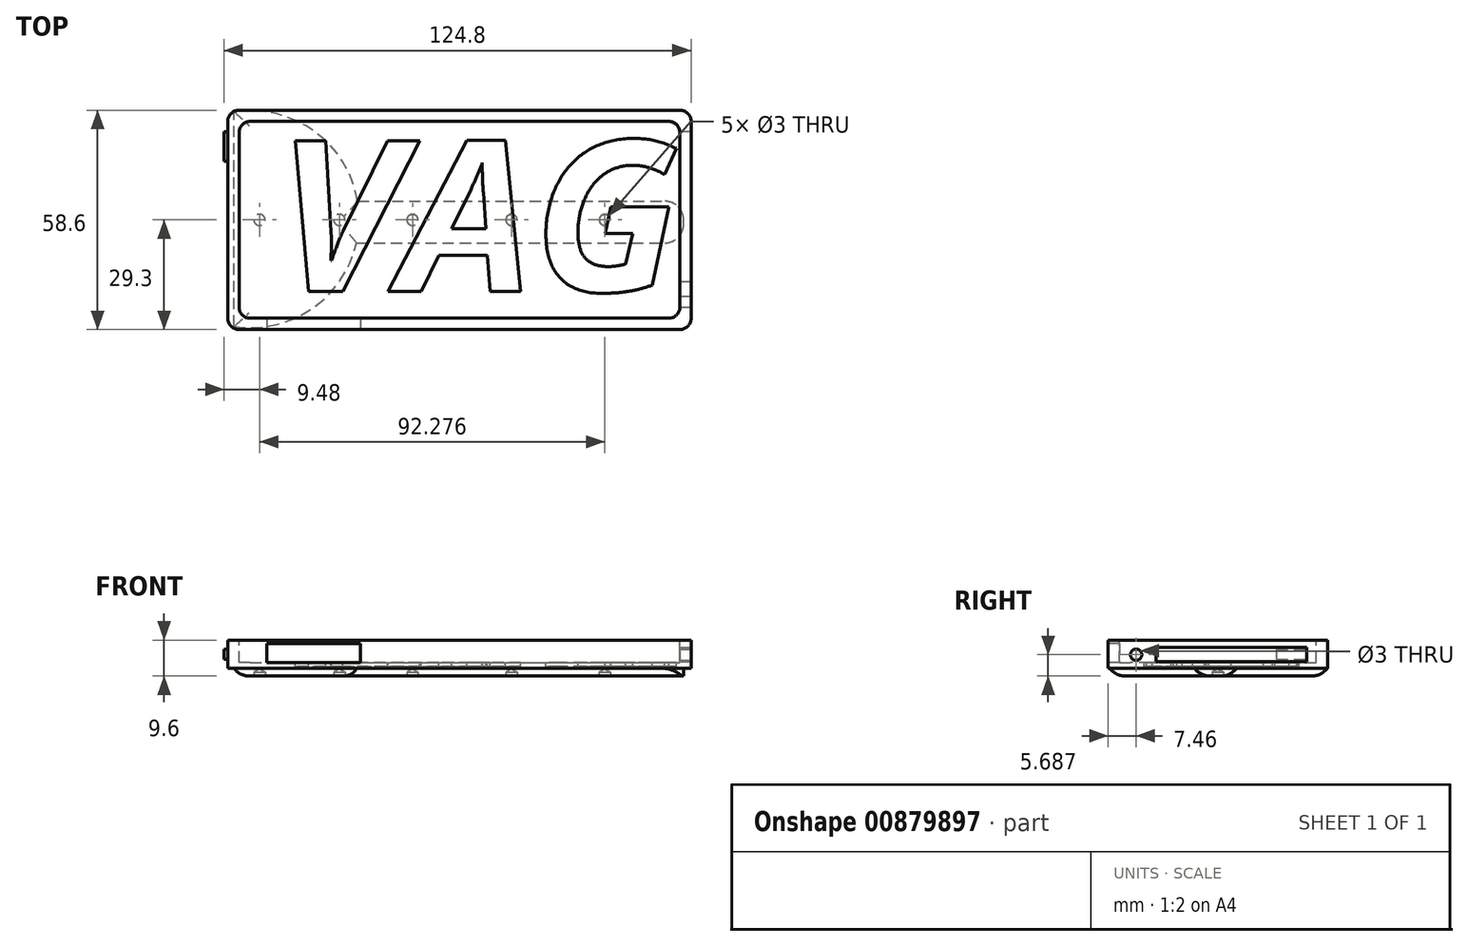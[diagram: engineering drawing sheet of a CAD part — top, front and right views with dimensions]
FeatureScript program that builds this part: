
annotation { "Feature Type Name" : "Feature", "Feature Type Description" : "" }
export const myFeature = defineFeature(function(context is Context, id is Id, definition is map)
    precondition{}
    {
        {
            var Q0;
            Q0=qCreatedBy(makeId("Top.planeOp"),FACE);
            var sketch = newSketch(context, id + "F0", { "sketchPlane" : qUnion([Q0])});
            skLineSegment(sketch, "E0.bottom", {"start": v(-118.8, 29.3) * mm, "end": v(-1, 29.3) * mm});
            skLineSegment(sketch, "E0.top", {"start": v(-118.8, -29.3) * mm, "end": v(-1, -29.3) * mm});
            skLineSegment(sketch, "E0.left", {"start": v(-121.8, 26.3) * mm, "end": v(-121.8, -26.3) * mm});
            skLineSegment(sketch, "E0.right", {"start": v(2, 26.3) * mm, "end": v(2, -26.3) * mm});
            skPoint(sketch, "E1.visualSharp", {"position": v(-121.8, 29.3) * mm});
            skArc(sketch, "E1.filletArc", {"start": v(-118.8, 29.3) * mm, "mid": v(-120.92, 28.42) * mm, "end": v(-121.8, 26.3) * mm});
            skPoint(sketch, "E2.visualSharp", {"position": v(2, 29.3) * mm});
            skArc(sketch, "E2.filletArc", {"start": v(2, 26.3) * mm, "mid": v(1.12, 28.42) * mm, "end": v(-1, 29.3) * mm});
            skPoint(sketch, "E3.visualSharp", {"position": v(2, -29.3) * mm});
            skArc(sketch, "E3.filletArc", {"start": v(-1, -29.3) * mm, "mid": v(1.12, -28.42) * mm, "end": v(2, -26.3) * mm});
            skPoint(sketch, "E4.visualSharp", {"position": v(-121.8, -29.3) * mm});
            skArc(sketch, "E4.filletArc", {"start": v(-121.8, -26.3) * mm, "mid": v(-120.92, -28.42) * mm, "end": v(-118.8, -29.3) * mm});
            skSolve(sketch);
        }
        {
            var Q0;
            Q0 = qSketchRegion(id + "F0", true);
            extrude(context, id + "F1", {"entities" : qUnion([Q0]), "depth" : 7.6 * mm, "offsetDistance" : 25 * mm});
        }
        {
            var Q0;
            Q0=makeQuery(id+"F1.opExtrude","CAP_FACE",FACE,{"disambiguationData":[OSD([sQuery(id+"F0.wireOp",EDGE,"E0.bottom"),sQuery(id+"F0.wireOp",EDGE,"E0.top"),sQuery(id+"F0.wireOp",EDGE,"E0.left"),sQuery(id+"F0.wireOp",EDGE,"E0.right"),sQuery(id+"F0.wireOp",EDGE,"E1.filletArc"),sQuery(id+"F0.wireOp",EDGE,"E2.filletArc"),sQuery(id+"F0.wireOp",EDGE,"E3.filletArc"),sQuery(id+"F0.wireOp",EDGE,"E4.filletArc")])],"isStart":false});
            var sketch = newSketch(context, id + "F2", { "sketchPlane" : qUnion([Q0])});
            skLineSegment(sketch, "E5.bottom", {"start": v(-115.8, 26.3) * mm, "end": v(-4, 26.3) * mm});
            skLineSegment(sketch, "E5.top", {"start": v(-115.8, -26.3) * mm, "end": v(-4, -26.3) * mm});
            skLineSegment(sketch, "E5.left", {"start": v(-118.8, 23.3) * mm, "end": v(-118.8, -23.3) * mm});
            skLineSegment(sketch, "E5.right", {"start": v(-1, 23.3) * mm, "end": v(-1, -23.3) * mm});
            skPoint(sketch, "E6.visualSharp", {"position": v(-1, 26.3) * mm});
            skArc(sketch, "E6.filletArc", {"start": v(-1, 23.3) * mm, "mid": v(-1.88, 25.42) * mm, "end": v(-4, 26.3) * mm});
            skPoint(sketch, "E7.visualSharp", {"position": v(-1, -26.3) * mm});
            skArc(sketch, "E7.filletArc", {"start": v(-4, -26.3) * mm, "mid": v(-1.88, -25.42) * mm, "end": v(-1, -23.3) * mm});
            skPoint(sketch, "E8.visualSharp", {"position": v(-118.8, -26.3) * mm});
            skArc(sketch, "E8.filletArc", {"start": v(-118.8, -23.3) * mm, "mid": v(-117.92, -25.42) * mm, "end": v(-115.8, -26.3) * mm});
            skPoint(sketch, "E9.visualSharp", {"position": v(-118.8, 26.3) * mm});
            skArc(sketch, "E9.filletArc", {"start": v(-115.8, 26.3) * mm, "mid": v(-117.92, 25.42) * mm, "end": v(-118.8, 23.3) * mm});
            skPoint(sketch, "E10.centerSnap0", {"position": v(-100.94, 0) * mm});
            skSolve(sketch);
        }
        {
            var Q0;
            Q0=makeQuery(id+"F2.imprint","IMPRINT",FACE,{"disambiguationData":[TD([[makeQuery(id+"F2.imprint","IMPRINT",EDGE,{"derivedFrom":sQuery(id+"F2.wireOp",EDGE,"E5.right")}),-1.0]])]});
            var Q1;
            Q1=makeQuery(id+"F2.imprint","IMPRINT",FACE,{"disambiguationData":[TD([[makeQuery(id+"F2.imprint","IMPRINT",EDGE,{"derivedFrom":sQuery(id+"F2.wireOp",EDGE,"E10")}),1.0]])]});
            var Q2;
            Q2=makeQuery(id+"F1.opExtrude","CAP_FACE",FACE,{"disambiguationData":[OSD([sQuery(id+"F0.wireOp",EDGE,"E0.bottom"),sQuery(id+"F0.wireOp",EDGE,"E0.top"),sQuery(id+"F0.wireOp",EDGE,"E0.left"),sQuery(id+"F0.wireOp",EDGE,"E0.right"),sQuery(id+"F0.wireOp",EDGE,"E1.filletArc"),sQuery(id+"F0.wireOp",EDGE,"E2.filletArc"),sQuery(id+"F0.wireOp",EDGE,"E3.filletArc"),sQuery(id+"F0.wireOp",EDGE,"E4.filletArc")])],"isStart":true});
            extrude(context, id + "F3", {"entities" : qUnion([Q0, Q1]), "operationType" : NewBodyOperationType.REMOVE, "oppositeDirection" : true, "depth" : 6 * mm, "endBoundEntityFace" : qUnion([Q2]), "offsetDistance" : 25 * mm});
        }
        {
            var Q0;
            Q0=makeQuery(id+"F1.opExtrude","SWEPT_FACE",FACE,{"disambiguationData":[OSD([sQuery(id+"F0.wireOp",EDGE,"E0.top")])]});
            var sketch = newSketch(context, id + "F4", { "sketchPlane" : qUnion([Q0])});
            skLineSegment(sketch, "E11.bottom", {"start": v(-111.33, 6.6) * mm, "end": v(-86.33, 6.6) * mm});
            skLineSegment(sketch, "E11.top", {"start": v(-111.33, 1.6) * mm, "end": v(-86.33, 1.6) * mm});
            skLineSegment(sketch, "E11.left", {"start": v(-111.33, 6.6) * mm, "end": v(-111.33, 1.6) * mm});
            skLineSegment(sketch, "E11.right", {"start": v(-86.33, 6.6) * mm, "end": v(-86.33, 1.6) * mm});
            skSolve(sketch);
        }
        {
            var Q0;
            Q0 = qSketchRegion(id + "F4", true);
            extrude(context, id + "F5", {"entities" : qUnion([Q0]), "operationType" : NewBodyOperationType.REMOVE, "oppositeDirection" : true, "depth" : 25 * mm, "offsetDistance" : 25 * mm});
        }
        {
            var Q0;
            Q0=makeQuery(id+"F1.opExtrude","SWEPT_FACE",FACE,{"disambiguationData":[OSD([sQuery(id+"F0.wireOp",EDGE,"E0.right")])]});
            var sketch = newSketch(context, id + "F6", { "sketchPlane" : qUnion([Q0])});
            skLineSegment(sketch, "E12.bottom", {"start": v(-16.48, 5.6) * mm, "end": v(23.7, 5.6) * mm});
            skLineSegment(sketch, "E12.top", {"start": v(-16.48, 1.77) * mm, "end": v(23.7, 1.77) * mm});
            skLineSegment(sketch, "E12.left", {"start": v(-16.48, 5.6) * mm, "end": v(-16.48, 1.77) * mm});
            skLineSegment(sketch, "E12.right", {"start": v(23.7, 5.6) * mm, "end": v(23.7, 1.77) * mm});
            skSolve(sketch);
        }
        {
            var Q0;
            Q0 = qSketchRegion(id + "F6", true);
            extrude(context, id + "F7", {"entities" : qUnion([Q0]), "operationType" : NewBodyOperationType.REMOVE, "oppositeDirection" : true, "depth" : 25 * mm, "offsetDistance" : 25 * mm});
        }
        {
            var Q0;
            Q0=makeQuery(id+"F1.opExtrude","SWEPT_FACE",FACE,{"disambiguationData":[OSD([sQuery(id+"F0.wireOp",EDGE,"E0.right")])]});
            var sketch = newSketch(context, id + "F8", { "sketchPlane" : qUnion([Q0])});
            skPoint(sketch, "E13", {"position": v(-21.84, 3.69) * mm});
            skPoint(sketch, "E13.positionSnap0", {"position": v(-16.48, 3.69) * mm});
            skSolve(sketch);
        }
        {
            var Q0;
            Q0=sQuery(id+"F8.wireOp",VERTEX,"E13");
            var Q1;
            Q1=makeQuery(id+"F1.opExtrude","SWEPT_BODY",BODY,{"disambiguationData":[OSD([sQuery(id+"F0.wireOp",EDGE,"E0.bottom"),sQuery(id+"F0.wireOp",EDGE,"E0.top"),sQuery(id+"F0.wireOp",EDGE,"E0.left"),sQuery(id+"F0.wireOp",EDGE,"E0.right"),sQuery(id+"F0.wireOp",EDGE,"E1.filletArc"),sQuery(id+"F0.wireOp",EDGE,"E2.filletArc"),sQuery(id+"F0.wireOp",EDGE,"E3.filletArc"),sQuery(id+"F0.wireOp",EDGE,"E4.filletArc")])]});
            hole(context, id + "F9", {"style" : HoleStyle.SIMPLE, "endStyle" : HoleEndStyle.BLIND, "holeDiameter" : 3 * mm, "majorDiameter" : 5 * mm, "holeDepth" : 20 * mm, "isTappedThrough" : true, "tappedDepth" : 12 * mm, "tapClearance" : 3, "locations" : qUnion([Q0]), "scope" : qUnion([Q1])});
        }
        {
            var Q0;
            Q0=makeQuery(id+"F1.opExtrude","SWEPT_FACE",FACE,{"disambiguationData":[OSD([sQuery(id+"F0.wireOp",EDGE,"E0.left")])]});
            var sketch = newSketch(context, id + "F10", { "sketchPlane" : qUnion([Q0])});
            skLineSegment(sketch, "E14.bottom", {"start": v(-15.7, 2.5) * mm, "end": v(-23.56, 2.5) * mm});
            skLineSegment(sketch, "E14.top", {"start": v(-15.7, 5.1) * mm, "end": v(-23.56, 5.1) * mm});
            skLineSegment(sketch, "E14.left", {"start": v(-15.7, 2.5) * mm, "end": v(-15.7, 5.1) * mm});
            skLineSegment(sketch, "E14.right", {"start": v(-23.56, 2.5) * mm, "end": v(-23.56, 5.1) * mm});
            skPoint(sketch, "E14.middle", {"position": v(-19.63, 3.8) * mm});
            skPoint(sketch, "E14.middle.positionSnap0", {"position": v(-26.3, 3.8) * mm});
            skPoint(sketch, "E14.centerSnap0", {"position": v(-26.3, 3.8) * mm});
            skSolve(sketch);
        }
        {
            var Q0;
            Q0 = qSketchRegion(id + "F10", true);
            extrude(context, id + "F11", {"entities" : qUnion([Q0]), "operationType" : NewBodyOperationType.ADD, "depth" : 1 * mm, "offsetDistance" : 25 * mm});
        }
        {
            var Q0;
            Q0=makeQuery(id+"F0.imprint","IMPRINT",FACE,{"disambiguationData":[TD([[makeQuery(id+"F0.imprint","IMPRINT",EDGE,{"derivedFrom":sQuery(id+"F0.wireOp",EDGE,"E0.bottom")}),-1.0]])]});
            var sketch = newSketch(context, id + "F12", { "sketchPlane" : qUnion([Q0])});
            skArc(sketch, "E15", {"start": v(-120.1, -28.48) * mm, "mid": v(-86.7, 0.18) * mm, "end": v(-120.1, 28.83) * mm});
            skLineSegment(sketch, "E16", {"start": v(-120.1, -28.48) * mm, "end": v(-120.1, 28.83) * mm});
            skSolve(sketch);
        }
        {
            var Q0;
            Q0 = qSketchRegion(id + "F12", true);
            extrude(context, id + "F13", {"entities" : qUnion([Q0]), "operationType" : NewBodyOperationType.ADD, "oppositeDirection" : true, "depth" : 2 * mm, "offsetDistance" : 25 * mm});
        }
        {
            var Q0;
            Q0=makeQuery(id+"F0.imprint","IMPRINT",FACE,{"disambiguationData":[TD([[makeQuery(id+"F0.imprint","IMPRINT",EDGE,{"derivedFrom":sQuery(id+"F0.wireOp",EDGE,"E0.bottom")}),-1.0]])]});
            var sketch = newSketch(context, id + "F14", { "sketchPlane" : qUnion([Q0])});
            skLineSegment(sketch, "E17.bottom", {"start": v(-91.98, -6.16) * mm, "end": v(0, -6.16) * mm});
            skLineSegment(sketch, "E17.top", {"start": v(-91.98, 4.96) * mm, "end": v(0, 4.96) * mm});
            skLineSegment(sketch, "E17.left", {"start": v(-91.98, -6.16) * mm, "end": v(-91.98, 4.96) * mm});
            skLineSegment(sketch, "E17.right", {"start": v(0, -6.16) * mm, "end": v(0, 4.96) * mm});
            skSolve(sketch);
        }
        {
            var Q0;
            Q0 = qSketchRegion(id + "F14", true);
            extrude(context, id + "F15", {"entities" : qUnion([Q0]), "operationType" : NewBodyOperationType.ADD, "oppositeDirection" : true, "depth" : 2 * mm, "offsetDistance" : 25 * mm});
        }
        {
            var Q0;
            Q0=makeQuery(id+"F15.boolean.opBoolean","MERGE",FACE,{"derivedFrom":[makeQuery(id+"F13.opExtrude","CAP_FACE",FACE,{"disambiguationData":[OSD([sQuery(id+"F12.wireOp",EDGE,"E15"),sQuery(id+"F12.wireOp",EDGE,"E16")])],"isStart":false}),makeQuery(id+"F15.opExtrude","CAP_FACE",FACE,{"disambiguationData":[OSD([sQuery(id+"F14.wireOp",EDGE,"E17.bottom"),sQuery(id+"F14.wireOp",EDGE,"E17.top"),sQuery(id+"F14.wireOp",EDGE,"E17.left"),sQuery(id+"F14.wireOp",EDGE,"E17.right")])],"isStart":false})]});
            var sketch = newSketch(context, id + "F16", { "sketchPlane" : qUnion([Q0])});
            skPoint(sketch, "E18", {"position": v(-113.32, 0) * mm});
            skPoint(sketch, "E19", {"position": v(-91.98, 0) * mm});
            skPoint(sketch, "E20", {"position": v(-72.44, 0) * mm});
            skPoint(sketch, "E21", {"position": v(-46, 0) * mm});
            skPoint(sketch, "E22", {"position": v(-21.04, 0) * mm});
            skSolve(sketch);
        }
        {
            var Q0;
            Q0=sQuery(id+"F16.wireOp",VERTEX,"E18");
            var Q1;
            Q1=sQuery(id+"F16.wireOp",VERTEX,"E19");
            var Q2;
            Q2=sQuery(id+"F16.wireOp",VERTEX,"E20");
            var Q3;
            Q3=sQuery(id+"F16.wireOp",VERTEX,"E21");
            var Q4;
            Q4=sQuery(id+"F16.wireOp",VERTEX,"E22");
            var Q5;
            Q5=makeQuery(id+"F1.opExtrude","SWEPT_BODY",BODY,{"disambiguationData":[OSD([sQuery(id+"F0.wireOp",EDGE,"E0.bottom"),sQuery(id+"F0.wireOp",EDGE,"E0.top"),sQuery(id+"F0.wireOp",EDGE,"E0.left"),sQuery(id+"F0.wireOp",EDGE,"E0.right"),sQuery(id+"F0.wireOp",EDGE,"E1.filletArc"),sQuery(id+"F0.wireOp",EDGE,"E2.filletArc"),sQuery(id+"F0.wireOp",EDGE,"E3.filletArc"),sQuery(id+"F0.wireOp",EDGE,"E4.filletArc")])]});
            hole(context, id + "F17", {"style" : HoleStyle.SIMPLE, "endStyle" : HoleEndStyle.BLIND, "holeDiameter" : 3 * mm, "majorDiameter" : 5 * mm, "holeDepth" : 1 * mm, "isTappedThrough" : true, "tappedDepth" : 12 * mm, "tapClearance" : 3, "locations" : qUnion([Q0, Q1, Q2, Q3, Q4]), "scope" : qUnion([Q5])});
        }
        {
            var Q0;
            Q0=makeQuery(id+"F15.opExtrude","SWEPT_EDGE",EDGE,{"disambiguationData":[OSD([sQuery(id+"F14.wireOp",EDGE,"E17.bottom"),sQuery(id+"F14.wireOp",EDGE,"E17.right")])]});
            var Q1;
            Q1=makeQuery(id+"F15.opExtrude","SWEPT_EDGE",EDGE,{"disambiguationData":[OSD([sQuery(id+"F14.wireOp",EDGE,"E17.top"),sQuery(id+"F14.wireOp",EDGE,"E17.right")])]});
            var Q2;
            Q2=makeQuery(id+"F15.opExtrude","CAP_EDGE",EDGE,{"disambiguationData":[OSD([sQuery(id+"F14.wireOp",EDGE,"E17.top")])],"isStart":false});
            var Q3;
            Q3=makeQuery(id+"F15.opExtrude","CAP_EDGE",EDGE,{"disambiguationData":[OSD([sQuery(id+"F14.wireOp",EDGE,"E17.bottom")])],"isStart":false});
            var Q4;
            Q4=makeQuery(id+"F13.opExtrude","CAP_EDGE",EDGE,{"disambiguationData":[OSD([sQuery(id+"F12.wireOp",EDGE,"E16")])],"isStart":false});
            var Q5;
            {var subQ0=sQuery(id+"F14.wireOp",EDGE,"E17.top");var subQ2=sQuery(id+"F12.wireOp",EDGE,"E15");Q5=makeQuery(id+"F15.boolean.opBoolean","SPLIT",EDGE,{"disambiguationData":[TD([makeQuery(id+"F15.opExtrude","SWEPT_FACE",FACE,{"disambiguationData":[OSD([subQ0])]})])],"derivedFrom":makeQuery(id+"F13.opExtrude","CAP_EDGE",EDGE,{"disambiguationData":[OSD([subQ2])],"isStart":false})});}
            var Q6;
            {var subQ0=sQuery(id+"F14.wireOp",EDGE,"E17.bottom");var subQ2=sQuery(id+"F12.wireOp",EDGE,"E15");Q6=makeQuery(id+"F15.boolean.opBoolean","SPLIT",EDGE,{"disambiguationData":[TD([makeQuery(id+"F15.opExtrude","SWEPT_FACE",FACE,{"disambiguationData":[OSD([subQ0])]})])],"derivedFrom":makeQuery(id+"F13.opExtrude","CAP_EDGE",EDGE,{"disambiguationData":[OSD([subQ2])],"isStart":false})});}
            fillet(context, id + "F18", {"entities" : qUnion([Q0, Q1, Q2, Q3, Q4, Q5, Q6]), "radius" : 5 * mm, "tangentPropagation" : true, "allowEdgeOverflow" : false});
        }
        {
            var Q0;
            Q0=makeQuery(id+"F3.boolean.opBoolean","COPY",FACE,{"derivedFrom":makeQuery(id+"F3.opExtrude","CAP_FACE",FACE,{"disambiguationData":[OSD([sQuery(id+"F2.wireOp",EDGE,"E5.bottom"),sQuery(id+"F2.wireOp",EDGE,"E5.top"),sQuery(id+"F2.wireOp",EDGE,"E5.left"),sQuery(id+"F2.wireOp",EDGE,"E5.right"),sQuery(id+"F2.wireOp",EDGE,"E6.filletArc"),sQuery(id+"F2.wireOp",EDGE,"E7.filletArc"),sQuery(id+"F2.wireOp",EDGE,"E8.filletArc"),sQuery(id+"F2.wireOp",EDGE,"E9.filletArc")])],"isStart":false})});
            var sketch = newSketch(context, id + "F19", { "sketchPlane" : qUnion([Q0])});
            skText(sketch, "E23", { "text": "VAG", "fontName": "OpenSans-BoldItalic.ttf"});
            const initialGuessF19  = {"E23": [-0.10881, -0.01909, 1, 0, 0.04058]};
            skSetInitialGuess(sketch, initialGuessF19);
            skSolve(sketch);
        }
        {
            var Q0;
            Q0 = qSketchRegion(id + "F19", true);
            extrude(context, id + "F20", {"entities" : qUnion([Q0]), "operationType" : NewBodyOperationType.REMOVE, "oppositeDirection" : true, "depth" : 1 * mm, "offsetDistance" : 25 * mm});
        }
    });
